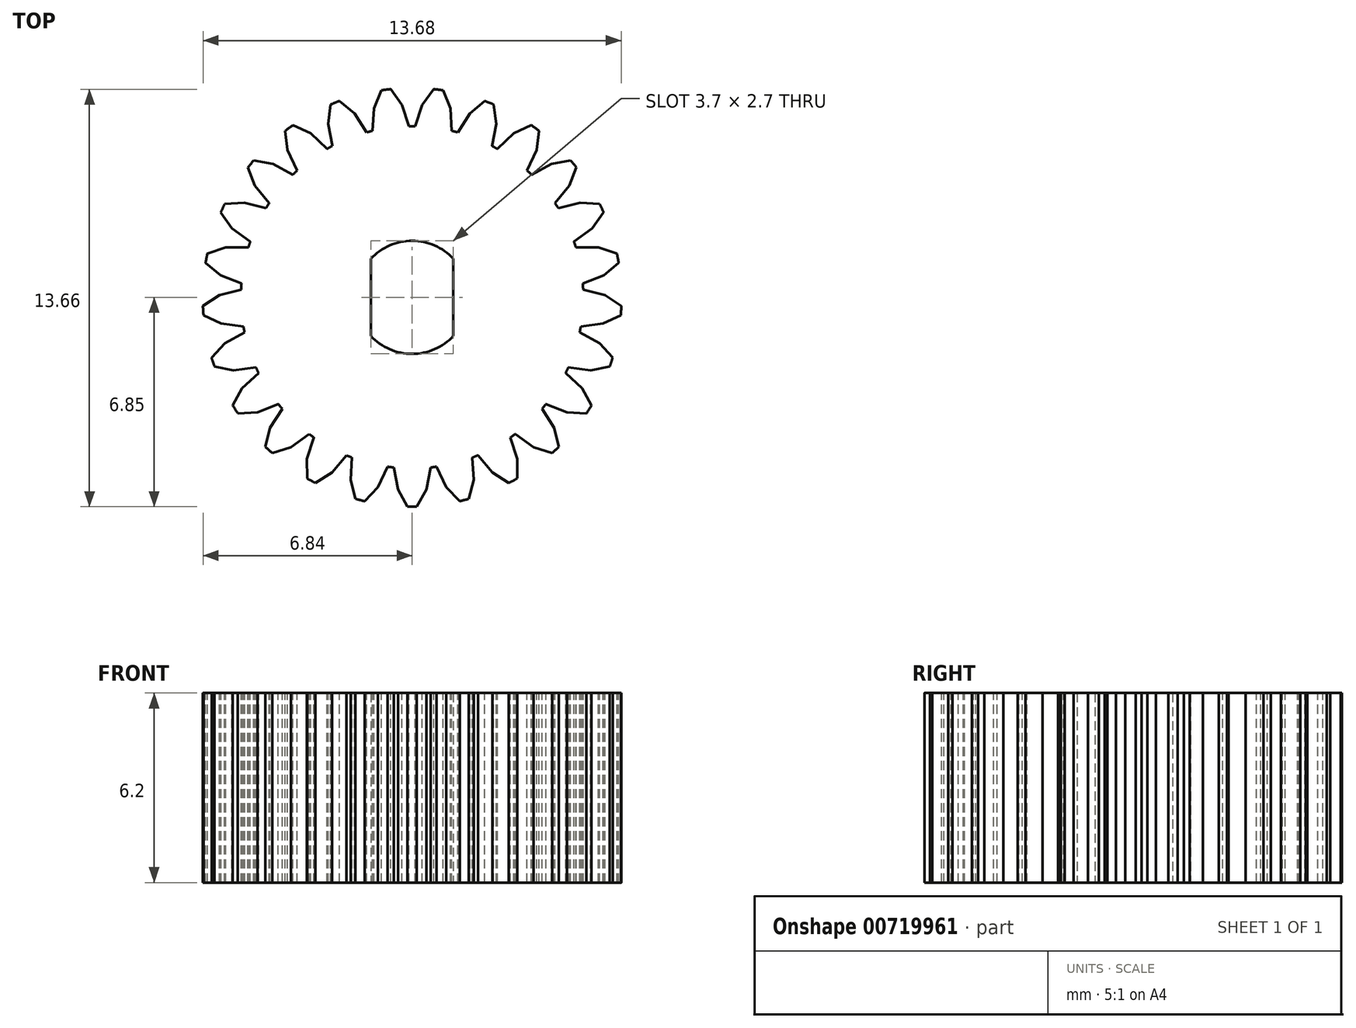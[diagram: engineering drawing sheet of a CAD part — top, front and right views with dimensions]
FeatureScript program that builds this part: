
annotation { "Feature Type Name" : "Feature", "Feature Type Description" : "" }
export const myFeature = defineFeature(function(context is Context, id is Id, definition is map)
    precondition{}
    {
        {
            var Q0;
            Q0=qCreatedBy(makeId("Top.planeOp"),FACE);
            var sketch = newSketch(context, id + "F0", { "sketchPlane" : qUnion([Q0])});
            skCircle(sketch, "E0", {"center": v(0, 0) * mm, "radius": 6.85 * mm});
            skArc(sketch, "E1", {"start": v(-1.35, -1.26) * mm, "mid": v(0, -1.85) * mm, "end": v(1.35, -1.26) * mm});
            skLineSegment(sketch, "E2.left", {"start": v(-1.35, 1.26) * mm, "end": v(-1.35, -1.26) * mm});
            skLineSegment(sketch, "E2.right", {"start": v(1.35, 1.26) * mm, "end": v(1.35, -1.26) * mm});
            skArc(sketch, "E3.trimOffspring", {"start": v(1.35, 1.26) * mm, "mid": v(0, 1.85) * mm, "end": v(-1.35, 1.26) * mm});
            skSolve(sketch);
        }
        {
            var Q0;
            Q0=qSketchRegion(id+"F0",true);
            extrude(context, id + "F1", {"entities" : qUnion([Q0]), "depth" : 6.2 * mm, "offsetDistance" : 25 * mm});
        }
        {
            var Q0;
            Q0=makeQuery(id+"F1.opExtrude","CAP_FACE",FACE,{"disambiguationData":[OSD([sQuery(id+"F0.wireOp",EDGE,"E0"),sQuery(id+"F0.wireOp",EDGE,"E1"),sQuery(id+"F0.wireOp",EDGE,"E2.left"),sQuery(id+"F0.wireOp",EDGE,"E2.right"),sQuery(id+"F0.wireOp",EDGE,"E3.trimOffspring")])],"isStart":false});
            var sketch = newSketch(context, id + "F2", { "sketchPlane" : qUnion([Q0])});
            skArc(sketch, "E4.0", {"start": v(0.7, 6.81) * mm, "mid": v(0, 6.85) * mm, "end": v(-0.7, 6.81) * mm});
            skPoint(sketch, "E5.orphan", {"position": v(0, 5.3) * mm});
            skArc(sketch, "E6.trimOffspring", {"start": v(0.1, 5.6) * mm, "mid": v(0, 5.6) * mm, "end": v(-0.1, 5.6) * mm});
            skLineSegment(sketch, "E7", {"start": v(-0.7, 6.81) * mm, "end": v(-0.33, 6.3) * mm});
            skLineSegment(sketch, "E8", {"start": v(-0.1, 5.6) * mm, "end": v(-0.33, 6.3) * mm});
            skLineSegment(sketch, "E9.MirrorCS", {"start": v(0.7, 6.81) * mm, "end": v(0.33, 6.3) * mm});
            skLineSegment(sketch, "E10.MirrorCS", {"start": v(0.1, 5.6) * mm, "end": v(0.33, 6.3) * mm});
            skLineSegment(sketch, "E11.1.0", {"start": v(-2.38, 6.42) * mm, "end": v(-1.88, 6.02) * mm});
            skArc(sketch, "E11.1.1", {"start": v(-1.01, 6.78) * mm, "mid": v(-1.7, 6.63) * mm, "end": v(-2.38, 6.42) * mm});
            skLineSegment(sketch, "E11.1.2", {"start": v(-1.01, 6.78) * mm, "end": v(-1.25, 6.18) * mm});
            skLineSegment(sketch, "E11.1.3", {"start": v(-1.3, 5.45) * mm, "end": v(-1.25, 6.18) * mm});
            skLineSegment(sketch, "E11.1.4", {"start": v(-1.49, 5.4) * mm, "end": v(-1.88, 6.02) * mm});
            skArc(sketch, "E11.1.5", {"start": v(-1.22, 5.47) * mm, "mid": v(-1.35, 5.43) * mm, "end": v(-1.49, 5.4) * mm});
            skLineSegment(sketch, "E11.2.0", {"start": v(-3.9, 5.63) * mm, "end": v(-3.32, 5.36) * mm});
            skArc(sketch, "E11.2.1", {"start": v(-2.66, 6.31) * mm, "mid": v(-3.3, 6) * mm, "end": v(-3.9, 5.63) * mm});
            skLineSegment(sketch, "E11.2.2", {"start": v(-2.66, 6.31) * mm, "end": v(-2.75, 5.68) * mm});
            skLineSegment(sketch, "E11.2.3", {"start": v(-2.6, 4.95) * mm, "end": v(-2.75, 5.68) * mm});
            skLineSegment(sketch, "E11.2.4", {"start": v(-2.78, 4.86) * mm, "end": v(-3.32, 5.36) * mm});
            skArc(sketch, "E11.2.5", {"start": v(-2.54, 5) * mm, "mid": v(-2.66, 4.93) * mm, "end": v(-2.78, 4.86) * mm});
            skLineSegment(sketch, "E11.3.0", {"start": v(-5.18, 4.48) * mm, "end": v(-4.55, 4.37) * mm});
            skArc(sketch, "E11.3.1", {"start": v(-4.15, 5.45) * mm, "mid": v(-4.69, 5) * mm, "end": v(-5.18, 4.48) * mm});
            skLineSegment(sketch, "E11.3.2", {"start": v(-4.15, 5.45) * mm, "end": v(-4.07, 4.82) * mm});
            skLineSegment(sketch, "E11.3.3", {"start": v(-3.76, 4.15) * mm, "end": v(-4.07, 4.82) * mm});
            skLineSegment(sketch, "E11.3.4", {"start": v(-3.9, 4.01) * mm, "end": v(-4.55, 4.37) * mm});
            skArc(sketch, "E11.3.5", {"start": v(-3.7, 4.2) * mm, "mid": v(-3.8, 4.1) * mm, "end": v(-3.9, 4.01) * mm});
            skLineSegment(sketch, "E11.4.0", {"start": v(-6.13, 3.05) * mm, "end": v(-5.5, 3.1) * mm});
            skArc(sketch, "E11.4.1", {"start": v(-5.37, 4.25) * mm, "mid": v(-5.78, 3.67) * mm, "end": v(-6.13, 3.05) * mm});
            skLineSegment(sketch, "E11.4.2", {"start": v(-5.37, 4.25) * mm, "end": v(-5.14, 3.65) * mm});
            skLineSegment(sketch, "E11.4.3", {"start": v(-4.67, 3.08) * mm, "end": v(-5.14, 3.65) * mm});
            skLineSegment(sketch, "E11.4.4", {"start": v(-4.78, 2.92) * mm, "end": v(-5.5, 3.1) * mm});
            skArc(sketch, "E11.4.5", {"start": v(-4.63, 3.15) * mm, "mid": v(-4.7, 3.03) * mm, "end": v(-4.78, 2.92) * mm});
            skLineSegment(sketch, "E11.5.0", {"start": v(-6.7, 1.43) * mm, "end": v(-6.1, 1.63) * mm});
            skArc(sketch, "E11.5.1", {"start": v(-6.26, 2.78) * mm, "mid": v(-6.51, 2.12) * mm, "end": v(-6.7, 1.43) * mm});
            skLineSegment(sketch, "E11.5.2", {"start": v(-6.26, 2.78) * mm, "end": v(-5.9, 2.26) * mm});
            skLineSegment(sketch, "E11.5.3", {"start": v(-5.3, 1.83) * mm, "end": v(-5.9, 2.26) * mm});
            skLineSegment(sketch, "E11.5.4", {"start": v(-5.36, 1.63) * mm, "end": v(-6.1, 1.63) * mm});
            skArc(sketch, "E11.5.5", {"start": v(-5.27, 1.9) * mm, "mid": v(-5.31, 1.77) * mm, "end": v(-5.36, 1.63) * mm});
            skLineSegment(sketch, "E11.6.0", {"start": v(-6.84, -0.28) * mm, "end": v(-6.3, 0.07) * mm});
            skArc(sketch, "E11.6.1", {"start": v(-6.76, 1.13) * mm, "mid": v(-6.84, 0.43) * mm, "end": v(-6.84, -0.28) * mm});
            skLineSegment(sketch, "E11.6.2", {"start": v(-6.76, 1.13) * mm, "end": v(-6.27, 0.72) * mm});
            skLineSegment(sketch, "E11.6.3", {"start": v(-5.58, 0.45) * mm, "end": v(-6.27, 0.72) * mm});
            skLineSegment(sketch, "E11.6.4", {"start": v(-5.6, 0.25) * mm, "end": v(-6.3, 0.07) * mm});
            skArc(sketch, "E11.6.5", {"start": v(-5.58, 0.53) * mm, "mid": v(-5.59, 0.4) * mm, "end": v(-5.6, 0.25) * mm});
            skLineSegment(sketch, "E11.7.0", {"start": v(-6.56, -1.97) * mm, "end": v(-6.13, -1.5) * mm});
            skArc(sketch, "E11.7.1", {"start": v(-6.83, -0.58) * mm, "mid": v(-6.73, -1.28) * mm, "end": v(-6.56, -1.97) * mm});
            skLineSegment(sketch, "E11.7.2", {"start": v(-6.83, -0.58) * mm, "end": v(-6.25, -0.86) * mm});
            skLineSegment(sketch, "E11.7.3", {"start": v(-5.52, -0.95) * mm, "end": v(-6.25, -0.86) * mm});
            skLineSegment(sketch, "E11.7.4", {"start": v(-5.48, -1.15) * mm, "end": v(-6.13, -1.5) * mm});
            skArc(sketch, "E11.7.5", {"start": v(-5.53, -0.87) * mm, "mid": v(-5.5, -1.01) * mm, "end": v(-5.48, -1.15) * mm});
            skLineSegment(sketch, "E11.8.0", {"start": v(-5.86, -3.54) * mm, "end": v(-5.56, -2.98) * mm});
            skArc(sketch, "E11.8.1", {"start": v(-6.47, -2.26) * mm, "mid": v(-6.2, -2.92) * mm, "end": v(-5.86, -3.54) * mm});
            skLineSegment(sketch, "E11.8.2", {"start": v(-6.47, -2.26) * mm, "end": v(-5.84, -2.39) * mm});
            skLineSegment(sketch, "E11.8.3", {"start": v(-5.1, -2.3) * mm, "end": v(-5.84, -2.39) * mm});
            skLineSegment(sketch, "E11.8.4", {"start": v(-5.02, -2.47) * mm, "end": v(-5.56, -2.98) * mm});
            skArc(sketch, "E11.8.5", {"start": v(-5.14, -2.22) * mm, "mid": v(-5.08, -2.35) * mm, "end": v(-5.02, -2.47) * mm});
            skLineSegment(sketch, "E11.9.0", {"start": v(-4.8, -4.89) * mm, "end": v(-4.65, -4.27) * mm});
            skArc(sketch, "E11.9.1", {"start": v(-5.7, -3.8) * mm, "mid": v(-5.28, -4.37) * mm, "end": v(-4.8, -4.89) * mm});
            skLineSegment(sketch, "E11.9.2", {"start": v(-5.7, -3.8) * mm, "end": v(-5.06, -3.76) * mm});
            skLineSegment(sketch, "E11.9.3", {"start": v(-4.38, -3.5) * mm, "end": v(-5.06, -3.76) * mm});
            skLineSegment(sketch, "E11.9.4", {"start": v(-4.25, -3.65) * mm, "end": v(-4.65, -4.27) * mm});
            skArc(sketch, "E11.9.5", {"start": v(-4.43, -3.43) * mm, "mid": v(-4.34, -3.54) * mm, "end": v(-4.25, -3.65) * mm});
            skLineSegment(sketch, "E11.10.0", {"start": v(-3.43, -5.93) * mm, "end": v(-3.44, -5.29) * mm});
            skArc(sketch, "E11.10.1", {"start": v(-4.58, -5.1) * mm, "mid": v(-4.03, -5.54) * mm, "end": v(-3.43, -5.93) * mm});
            skLineSegment(sketch, "E11.10.2", {"start": v(-4.58, -5.1) * mm, "end": v(-3.97, -4.9) * mm});
            skLineSegment(sketch, "E11.10.3", {"start": v(-3.37, -4.47) * mm, "end": v(-3.97, -4.9) * mm});
            skLineSegment(sketch, "E11.10.4", {"start": v(-3.2, -4.59) * mm, "end": v(-3.44, -5.29) * mm});
            skArc(sketch, "E11.10.5", {"start": v(-3.43, -4.42) * mm, "mid": v(-3.32, -4.5) * mm, "end": v(-3.2, -4.59) * mm});
            skLineSegment(sketch, "E11.11.0", {"start": v(-1.85, -6.6) * mm, "end": v(-2.01, -5.98) * mm});
            skArc(sketch, "E11.11.1", {"start": v(-3.16, -6.08) * mm, "mid": v(-2.52, -6.37) * mm, "end": v(-1.85, -6.6) * mm});
            skLineSegment(sketch, "E11.11.2", {"start": v(-3.16, -6.08) * mm, "end": v(-2.62, -5.74) * mm});
            skLineSegment(sketch, "E11.11.3", {"start": v(-2.15, -5.17) * mm, "end": v(-2.62, -5.74) * mm});
            skLineSegment(sketch, "E11.11.4", {"start": v(-1.97, -5.24) * mm, "end": v(-2.01, -5.98) * mm});
            skArc(sketch, "E11.11.5", {"start": v(-2.23, -5.14) * mm, "mid": v(-2.1, -5.2) * mm, "end": v(-1.97, -5.24) * mm});
            skLineSegment(sketch, "E11.12.0", {"start": v(-0.15, -6.85) * mm, "end": v(-0.46, -6.3) * mm});
            skArc(sketch, "E11.12.1", {"start": v(-1.55, -6.67) * mm, "mid": v(-0.86, -6.8) * mm, "end": v(-0.15, -6.85) * mm});
            skLineSegment(sketch, "E11.12.2", {"start": v(-1.55, -6.67) * mm, "end": v(-1.12, -6.2) * mm});
            skLineSegment(sketch, "E11.12.3", {"start": v(-0.8, -5.54) * mm, "end": v(-1.12, -6.2) * mm});
            skLineSegment(sketch, "E11.12.4", {"start": v(-0.6, -5.57) * mm, "end": v(-0.46, -6.3) * mm});
            skArc(sketch, "E11.12.5", {"start": v(-0.88, -5.53) * mm, "mid": v(-0.74, -5.55) * mm, "end": v(-0.6, -5.57) * mm});
            skLineSegment(sketch, "E11.13.0", {"start": v(1.55, -6.67) * mm, "end": v(1.12, -6.2) * mm});
            skArc(sketch, "E11.13.1", {"start": v(0.15, -6.85) * mm, "mid": v(0.86, -6.8) * mm, "end": v(1.55, -6.67) * mm});
            skLineSegment(sketch, "E11.13.2", {"start": v(0.15, -6.85) * mm, "end": v(0.46, -6.3) * mm});
            skLineSegment(sketch, "E11.13.3", {"start": v(0.6, -5.57) * mm, "end": v(0.46, -6.3) * mm});
            skLineSegment(sketch, "E11.13.4", {"start": v(0.8, -5.54) * mm, "end": v(1.12, -6.2) * mm});
            skArc(sketch, "E11.13.5", {"start": v(0.52, -5.58) * mm, "mid": v(0.66, -5.56) * mm, "end": v(0.8, -5.54) * mm});
            skLineSegment(sketch, "E11.14.0", {"start": v(3.16, -6.08) * mm, "end": v(2.62, -5.74) * mm});
            skArc(sketch, "E11.14.1", {"start": v(1.85, -6.6) * mm, "mid": v(2.52, -6.37) * mm, "end": v(3.16, -6.08) * mm});
            skLineSegment(sketch, "E11.14.2", {"start": v(1.85, -6.6) * mm, "end": v(2.01, -5.98) * mm});
            skLineSegment(sketch, "E11.14.3", {"start": v(1.97, -5.24) * mm, "end": v(2.01, -5.98) * mm});
            skLineSegment(sketch, "E11.14.4", {"start": v(2.15, -5.17) * mm, "end": v(2.62, -5.74) * mm});
            skArc(sketch, "E11.14.5", {"start": v(1.9, -5.27) * mm, "mid": v(2.03, -5.22) * mm, "end": v(2.15, -5.17) * mm});
            skLineSegment(sketch, "E11.15.0", {"start": v(4.58, -5.1) * mm, "end": v(3.97, -4.9) * mm});
            skArc(sketch, "E11.15.1", {"start": v(3.43, -5.93) * mm, "mid": v(4.03, -5.54) * mm, "end": v(4.58, -5.1) * mm});
            skLineSegment(sketch, "E11.15.2", {"start": v(3.43, -5.93) * mm, "end": v(3.44, -5.29) * mm});
            skLineSegment(sketch, "E11.15.3", {"start": v(3.2, -4.59) * mm, "end": v(3.44, -5.29) * mm});
            skLineSegment(sketch, "E11.15.4", {"start": v(3.37, -4.47) * mm, "end": v(3.97, -4.9) * mm});
            skArc(sketch, "E11.15.5", {"start": v(3.15, -4.63) * mm, "mid": v(3.26, -4.55) * mm, "end": v(3.37, -4.47) * mm});
            skLineSegment(sketch, "E11.16.0", {"start": v(5.7, -3.8) * mm, "end": v(5.06, -3.76) * mm});
            skArc(sketch, "E11.16.1", {"start": v(4.8, -4.89) * mm, "mid": v(5.28, -4.37) * mm, "end": v(5.7, -3.8) * mm});
            skLineSegment(sketch, "E11.16.2", {"start": v(4.8, -4.89) * mm, "end": v(4.65, -4.27) * mm});
            skLineSegment(sketch, "E11.16.3", {"start": v(4.25, -3.65) * mm, "end": v(4.65, -4.27) * mm});
            skLineSegment(sketch, "E11.16.4", {"start": v(4.38, -3.5) * mm, "end": v(5.06, -3.76) * mm});
            skArc(sketch, "E11.16.5", {"start": v(4.2, -3.7) * mm, "mid": v(4.29, -3.6) * mm, "end": v(4.38, -3.5) * mm});
            skLineSegment(sketch, "E11.17.0", {"start": v(6.47, -2.26) * mm, "end": v(5.84, -2.39) * mm});
            skArc(sketch, "E11.17.1", {"start": v(5.86, -3.54) * mm, "mid": v(6.2, -2.92) * mm, "end": v(6.47, -2.26) * mm});
            skLineSegment(sketch, "E11.17.2", {"start": v(5.86, -3.54) * mm, "end": v(5.56, -2.98) * mm});
            skLineSegment(sketch, "E11.17.3", {"start": v(5.02, -2.47) * mm, "end": v(5.56, -2.98) * mm});
            skLineSegment(sketch, "E11.17.4", {"start": v(5.1, -2.3) * mm, "end": v(5.84, -2.39) * mm});
            skArc(sketch, "E11.17.5", {"start": v(4.99, -2.54) * mm, "mid": v(5.05, -2.42) * mm, "end": v(5.1, -2.3) * mm});
            skLineSegment(sketch, "E11.18.0", {"start": v(6.83, -0.58) * mm, "end": v(6.25, -0.86) * mm});
            skArc(sketch, "E11.18.1", {"start": v(6.56, -1.97) * mm, "mid": v(6.73, -1.28) * mm, "end": v(6.83, -0.58) * mm});
            skLineSegment(sketch, "E11.18.2", {"start": v(6.56, -1.97) * mm, "end": v(6.13, -1.5) * mm});
            skLineSegment(sketch, "E11.18.3", {"start": v(5.48, -1.15) * mm, "end": v(6.13, -1.5) * mm});
            skLineSegment(sketch, "E11.18.4", {"start": v(5.52, -0.95) * mm, "end": v(6.25, -0.86) * mm});
            skArc(sketch, "E11.18.5", {"start": v(5.47, -1.22) * mm, "mid": v(5.5, -1.09) * mm, "end": v(5.52, -0.95) * mm});
            skLineSegment(sketch, "E11.19.0", {"start": v(6.76, 1.13) * mm, "end": v(6.27, 0.72) * mm});
            skArc(sketch, "E11.19.1", {"start": v(6.84, -0.28) * mm, "mid": v(6.84, 0.43) * mm, "end": v(6.76, 1.13) * mm});
            skLineSegment(sketch, "E11.19.2", {"start": v(6.84, -0.28) * mm, "end": v(6.3, 0.07) * mm});
            skLineSegment(sketch, "E11.19.3", {"start": v(5.6, 0.25) * mm, "end": v(6.3, 0.07) * mm});
            skLineSegment(sketch, "E11.19.4", {"start": v(5.58, 0.45) * mm, "end": v(6.27, 0.72) * mm});
            skArc(sketch, "E11.19.5", {"start": v(5.6, 0.17) * mm, "mid": v(5.6, 0.31) * mm, "end": v(5.58, 0.45) * mm});
            skLineSegment(sketch, "E11.20.0", {"start": v(6.26, 2.78) * mm, "end": v(5.9, 2.26) * mm});
            skArc(sketch, "E11.20.1", {"start": v(6.7, 1.43) * mm, "mid": v(6.51, 2.12) * mm, "end": v(6.26, 2.78) * mm});
            skLineSegment(sketch, "E11.20.2", {"start": v(6.7, 1.43) * mm, "end": v(6.1, 1.63) * mm});
            skLineSegment(sketch, "E11.20.3", {"start": v(5.36, 1.63) * mm, "end": v(6.1, 1.63) * mm});
            skLineSegment(sketch, "E11.20.4", {"start": v(5.3, 1.83) * mm, "end": v(5.9, 2.26) * mm});
            skArc(sketch, "E11.20.5", {"start": v(5.38, 1.56) * mm, "mid": v(5.34, 1.7) * mm, "end": v(5.3, 1.83) * mm});
            skLineSegment(sketch, "E11.21.0", {"start": v(5.37, 4.25) * mm, "end": v(5.14, 3.65) * mm});
            skArc(sketch, "E11.21.1", {"start": v(6.13, 3.05) * mm, "mid": v(5.78, 3.67) * mm, "end": v(5.37, 4.25) * mm});
            skLineSegment(sketch, "E11.21.2", {"start": v(6.13, 3.05) * mm, "end": v(5.5, 3.1) * mm});
            skLineSegment(sketch, "E11.21.3", {"start": v(4.78, 2.92) * mm, "end": v(5.5, 3.1) * mm});
            skLineSegment(sketch, "E11.21.4", {"start": v(4.67, 3.08) * mm, "end": v(5.14, 3.65) * mm});
            skArc(sketch, "E11.21.5", {"start": v(4.82, 2.85) * mm, "mid": v(4.75, 2.97) * mm, "end": v(4.67, 3.08) * mm});
            skLineSegment(sketch, "E11.22.0", {"start": v(4.15, 5.45) * mm, "end": v(4.07, 4.82) * mm});
            skArc(sketch, "E11.22.1", {"start": v(5.18, 4.48) * mm, "mid": v(4.69, 5) * mm, "end": v(4.15, 5.45) * mm});
            skLineSegment(sketch, "E11.22.2", {"start": v(5.18, 4.48) * mm, "end": v(4.55, 4.37) * mm});
            skLineSegment(sketch, "E11.22.3", {"start": v(3.9, 4.01) * mm, "end": v(4.55, 4.37) * mm});
            skLineSegment(sketch, "E11.22.4", {"start": v(3.76, 4.15) * mm, "end": v(4.07, 4.82) * mm});
            skArc(sketch, "E11.22.5", {"start": v(3.96, 3.96) * mm, "mid": v(3.86, 4.06) * mm, "end": v(3.76, 4.15) * mm});
            skLineSegment(sketch, "E11.23.0", {"start": v(2.66, 6.31) * mm, "end": v(2.75, 5.68) * mm});
            skArc(sketch, "E11.23.1", {"start": v(3.9, 5.63) * mm, "mid": v(3.3, 6) * mm, "end": v(2.66, 6.31) * mm});
            skLineSegment(sketch, "E11.23.2", {"start": v(3.9, 5.63) * mm, "end": v(3.32, 5.36) * mm});
            skLineSegment(sketch, "E11.23.3", {"start": v(2.78, 4.86) * mm, "end": v(3.32, 5.36) * mm});
            skLineSegment(sketch, "E11.23.4", {"start": v(2.6, 4.95) * mm, "end": v(2.75, 5.68) * mm});
            skArc(sketch, "E11.23.5", {"start": v(2.85, 4.82) * mm, "mid": v(2.73, 4.89) * mm, "end": v(2.6, 4.95) * mm});
            skLineSegment(sketch, "E11.24.0", {"start": v(1.01, 6.78) * mm, "end": v(1.25, 6.18) * mm});
            skArc(sketch, "E11.24.1", {"start": v(2.38, 6.42) * mm, "mid": v(1.7, 6.63) * mm, "end": v(1.01, 6.78) * mm});
            skLineSegment(sketch, "E11.24.2", {"start": v(2.38, 6.42) * mm, "end": v(1.88, 6.02) * mm});
            skLineSegment(sketch, "E11.24.3", {"start": v(1.49, 5.4) * mm, "end": v(1.88, 6.02) * mm});
            skLineSegment(sketch, "E11.24.4", {"start": v(1.3, 5.45) * mm, "end": v(1.25, 6.18) * mm});
            skArc(sketch, "E11.24.5", {"start": v(1.56, 5.38) * mm, "mid": v(1.43, 5.41) * mm, "end": v(1.3, 5.45) * mm});
            skPoint(sketch, "E12.orphan", {"position": v(0.18, 5.6) * mm});
            skSolve(sketch);
        }
        {
            var Q0;
            Q0=qSketchRegion(id+"F2",true);
            extrude(context, id + "F3", {"entities" : qUnion([Q0]), "operationType" : NewBodyOperationType.REMOVE, "oppositeDirection" : true, "depth" : 25 * mm, "offsetDistance" : 25 * mm});
        }
    });
